FCSTD DOCUMENT  (FreeCAD 0.16R6706 (Git))
Label: side-mount-btm
License: All rights reserved
LicenseURL: http://en.wikipedia.org/wiki/All_rights_reserved
objects: Sketcher::SketchObject×17, PartDesign::Pocket×17, App::DocumentObjectGroup×7, PartDesign::Fillet×7, Part::Box×5, Mesh::Feature×4
note: 63 computed .brp shape members not serialized (recipe doc carries the construction recipe); baked Part::Feature solids carry a one-line shape summary decoded from their .brp

FEATURE [Part::Box] Box  label="Cube"
  Height = 16.1
  Length = 52
  Width = 38
FEATURE [Sketcher::SketchObject] Sketch003  label="rail holes"
  Placement = pos=(0,38,0) rot=(0,0.707107,0.707107;3.14159rad)
  Support = -> Box [Face4]
  sketch-geometry (6):
    g0: Circle CenterX=-46 CenterY=8.25 CenterZ=0 NormalX=0 NormalY=0 NormalZ=1 Radius=4.2
    g1: Circle CenterX=-6 CenterY=8.25 CenterZ=0 NormalX=0 NormalY=0 NormalZ=1 Radius=4.2
    g2: LineSegment StartX=-35.5 StartY=13.1 StartZ=0 EndX=-16.5 EndY=13.1 EndZ=0
    g3: LineSegment StartX=-16.5 StartY=13.1 StartZ=0 EndX=-16.5 EndY=3.1 EndZ=0
    g4: LineSegment StartX=-16.5 StartY=3.1 StartZ=0 EndX=-35.5 EndY=3.1 EndZ=0
    g5: LineSegment StartX=-35.5 StartY=3.1 StartZ=0 EndX=-35.5 EndY=13.1 EndZ=0
  constraints (18):
    c: Equal(g1,g0)
    c: Radius(g0) = 4.2
    c: Distance(g0,g1) = 40
    c: DistanceY(g-1,g0) = 8.25
    c: DistanceY(g-1,g1) = 8.25
    c: DistanceX(g-2,g1) = -6
    c: Coincident(g2,g3)
    c: Coincident(g3,g4)
    c: Coincident(g4,g5)
    c: Coincident(g5,g2)
    c: Horizontal(g2)
    c: Horizontal(g4)
    c: Vertical(g3)
    c: Vertical(g5)
    c: Distance(g4) = 19
    c: DistanceX(g-2,g2) = -16.5
    c: DistanceY(g-1,g3) = 3.1
    c: Distance(g2,g4) = 10
FEATURE [PartDesign::Pocket] Pocket
  Length = 5
  Sketch = -> Sketch003
  Type = 1
FEATURE [Sketcher::SketchObject] Sketch007  label="mounting holes"
  Placement = pos=(0,0,16.1) rot=(0,0,1;0rad)
  Support = -> Pocket [Face3]
  sketch-geometry (4):
    g0: Circle CenterX=13 CenterY=5 CenterZ=0 NormalX=0 NormalY=0 NormalZ=1 Radius=1.4
    g1: Circle CenterX=39 CenterY=5 CenterZ=0 NormalX=0 NormalY=0 NormalZ=1 Radius=1.4
    g2: Circle CenterX=39 CenterY=33 CenterZ=0 NormalX=0 NormalY=0 NormalZ=1 Radius=1.4
    g3: Circle CenterX=13 CenterY=33 CenterZ=0 NormalX=0 NormalY=0 NormalZ=1 Radius=1.4
  constraints (12):
    c: Radius(g1) = 1.4
    c: Equal(g1,g0)
    c: Equal(g0,g3)
    c: Equal(g3,g2)
    c: DistanceY(g-1,g1) = 5
    c: DistanceY(g-1,g0) = 5
    c: DistanceX(g-2,g0) = 13
    c: DistanceX(g-2,g3) = 13
    c: Distance(g0,g3) = 28
    c: Distance(g1,g2) = 28
    c: Distance(g0,g1) = 26
    c: Distance(g3,g2) = 26
FEATURE [PartDesign::Pocket] Pocket001
  Length = 8
  Sketch = -> Sketch007
  Type = 1
FEATURE [Sketcher::SketchObject] Sketch008  label="rail set screw holes2"
  Placement = pos=(0,0,0) rot=(0.57735,-0.57735,-0.57735;2.0944rad)
  Support = -> Pocket001 [Face1]
  sketch-geometry (2):
    g0: Circle CenterX=-29.5 CenterY=8.25 CenterZ=0 NormalX=0 NormalY=0 NormalZ=1 Radius=1.5
    g1: Circle CenterX=-9.5 CenterY=8.25 CenterZ=0 NormalX=0 NormalY=0 NormalZ=1 Radius=1.5
  constraints (6):
    c: Radius(g0) = 1.5
    c: Equal(g0,g1)
    c: DistanceY(g-1,g0) = 8.25
    c: DistanceY(g-1,g1) = 8.25
    c: Distance(g0,g1) = 20
    c: DistanceX(g-2,g1) = -9.5
FEATURE [PartDesign::Pocket] Pocket002
  Length = 3
  Sketch = -> Sketch008
  Type = 0
FEATURE [Sketcher::SketchObject] Sketch004  label="rail set screw holes"
  Placement = pos=(52,0,0) rot=(0.57735,0.57735,0.57735;2.0944rad)
  Support = -> Pocket002 [Face8]
  sketch-geometry (2):
    g0: Circle CenterX=9.5 CenterY=8.25 CenterZ=0 NormalX=0 NormalY=0 NormalZ=1 Radius=1.5
    g1: Circle CenterX=29.5 CenterY=8.25 CenterZ=0 NormalX=0 NormalY=0 NormalZ=1 Radius=1.5
  constraints (6):
    c: Radius(g0) = 1.5
    c: Equal(g0,g1)
    c: DistanceY(g-1,g0) = 8.25
    c: DistanceY(g-1,g1) = 8.25
    c: Distance(g0,g1) = 20
    c: DistanceX(g-2,g0) = 9.5
FEATURE [PartDesign::Pocket] Pocket003
  Length = 3
  Sketch = -> Sketch004
  Type = 0
FEATURE [Sketcher::SketchObject] Sketch013  label="pulley hole"
  Placement = pos=(0,0,16.1) rot=(0,0,1;0rad)
  Support = -> Pocket003 [Face3]
  sketch-geometry (1):
    g0: Circle CenterX=26 CenterY=4 CenterZ=0 NormalX=0 NormalY=0 NormalZ=1 Radius=1.68
  constraints (3):
    c: DistanceX(g-2,g0) = 26
    c: DistanceY(g-1,g0) = 4
    c: Radius(g0) = 1.68
FEATURE [PartDesign::Pocket] Pocket004
  Length = 5
  Sketch = -> Sketch013
  Type = 1
FEATURE [Mesh::Feature] side_mnt_top  label="side-mnt-top"
  Placement = pos=(4.5,-38,16) rot=(0,0,1;0rad)
FEATURE [Mesh::Feature] side_mnt_top001  label="side-mnt-top001"
  Placement = pos=(30.5,-38,16) rot=(0,0,1;0rad)
FEATURE [App::DocumentObjectGroup] Group002  label="bearing mounts"
  Group = -> [side_mnt_top,side_mnt_top001]
FEATURE [Part::Box] Box001  label="pulley block"
  Height = 13
  Length = 36
  Placement = pos=(8,-13,-13) rot=(0,0,1;0rad)
  Width = 25
FEATURE [Sketcher::SketchObject] Sketch
  Placement = pos=(8,-13,-13) rot=(1,0,0;3.14159rad)
  Support = -> Box001 [Face5]
  sketch-geometry (3):
    g0: Circle CenterX=31 CenterY=-18 CenterZ=0 NormalX=0 NormalY=0 NormalZ=1 Radius=1.68
    g1: Circle CenterX=5 CenterY=-18 CenterZ=0 NormalX=0 NormalY=0 NormalZ=1 Radius=1.68
    g2: Circle CenterX=18 CenterY=-3.8 CenterZ=0 NormalX=0 NormalY=0 NormalZ=1 Radius=1.68
  constraints (9):
    c: Radius(g1) = 1.68
    c: Equal(g1,g0)
    c: DistanceX(g-2,g1) = 5
    c: DistanceY(g-1,g1) = -18
    c: DistanceY(g-1,g0) = -18
    c: Distance(g1,g0) = 26
    c: Equal(g2,g1)
    c: DistanceX(g-2,g2) = 18
    c: DistanceY(g-1,g2) = -3.8
FEATURE [PartDesign::Pocket] Pocket005
  Length = 5
  Placement = pos=(8,-13,-13) rot=(0,0,1;0rad)
  Sketch = -> Sketch
  Type = 1
FEATURE [Sketcher::SketchObject] Sketch014
  Placement = pos=(8,-13,-13) rot=(0.57735,-0.57735,-0.57735;2.0944rad)
  Support = -> Pocket005 [Face1]
  sketch-geometry (4):
    g0: LineSegment StartX=-13 StartY=13 StartZ=0 EndX=0 EndY=13 EndZ=0
    g1: LineSegment StartX=0 StartY=13 StartZ=0 EndX=0 EndY=3 EndZ=0
    g2: LineSegment StartX=0 StartY=3 StartZ=0 EndX=-13 EndY=3 EndZ=0
    g3: LineSegment StartX=-13 StartY=3 StartZ=0 EndX=-13 EndY=13 EndZ=0
  constraints (12):
    c: Coincident(g0,g1)
    c: Coincident(g1,g2)
    c: Coincident(g2,g3)
    c: Coincident(g3,g0)
    c: Horizontal(g0)
    c: Horizontal(g2)
    c: Vertical(g1)
    c: Vertical(g3)
    c: DistanceY(g-1,g1) = 3
    c: DistanceX(g-2,g0) = 0
    c: Distance(g3) = 10
    c: Distance(g0) = 13
FEATURE [PartDesign::Pocket] Pocket006
  Length = 5
  Placement = pos=(8,-13,-13) rot=(0,0,1;0rad)
  Sketch = -> Sketch014
  Type = 1
FEATURE [Sketcher::SketchObject] Sketch015
  Placement = pos=(8,-13,-13) rot=(1,0,0;3.14159rad)
  Support = -> Pocket006 [Face7]
  sketch-geometry (2):
    g0: Circle CenterX=5 CenterY=-18 CenterZ=0 NormalX=0 NormalY=0 NormalZ=1 Radius=3
    g1: Circle CenterX=31 CenterY=-18 CenterZ=0 NormalX=0 NormalY=0 NormalZ=1 Radius=3
  constraints (6):
    c: Distance(g0,g1) = 26
    c: Radius(g0) = 3
    c: Equal(g0,g1)
    c: DistanceX(g-2,g0) = 5
    c: DistanceY(g-1,g0) = -18
    c: DistanceY(g-1,g1) = -18
FEATURE [PartDesign::Pocket] Pocket007  label="countersinks"
  Length = 4
  Placement = pos=(8,-13,-13) rot=(0,0,1;0rad)
  Sketch = -> Sketch015
  Type = 0
FEATURE [Sketcher::SketchObject] Sketch016
  Placement = pos=(8,-13,0) rot=(0,0,1;0rad)
  Support = -> Pocket007 [Face5]
  sketch-geometry (3):
    g0: LineSegment StartX=8.5 StartY=13 StartZ=0 EndX=18 EndY=22 EndZ=0
    g1: LineSegment StartX=18 StartY=22 StartZ=0 EndX=27.5 EndY=13 EndZ=0
    g2: LineSegment StartX=27.5 StartY=13 StartZ=0 EndX=8.5 EndY=13 EndZ=0
  constraints (9):
    c: Coincident(g0,g1)
    c: Coincident(g1,g2)
    c: Coincident(g2,g0)
    c: Distance(g2) = 19
    c: DistanceX(g-2,g2) = 8.5
    c: DistanceY(g-1,g0) = 13
    c: DistanceX(g-2,g0) = 18
    c: DistanceY(g-1,g0) = 22
    c: DistanceY(g-1,g1) = 13
FEATURE [PartDesign::Pocket] Pocket008
  Length = 10
  Placement = pos=(8,-13,-13) rot=(0,0,1;0rad)
  Sketch = -> Sketch016
  Type = 0
FEATURE [PartDesign::Fillet] Fillet
  Base = -> Pocket008 [Edge16,Edge33]
  Placement = pos=(8,-13,-13) rot=(0,0,1;0rad)
  Radius = 18
FEATURE [PartDesign::Fillet] Fillet001
  Base = -> Fillet [Edge39]
  Placement = pos=(8,-13,-13) rot=(0,0,1;0rad)
  Radius = 4.5
FEATURE [PartDesign::Fillet] Fillet002
  Base = -> Fillet001 [Edge37,Edge34]
  Placement = pos=(8,-13,-13) rot=(0,0,1;0rad)
  Radius = 13.9
FEATURE [App::DocumentObjectGroup] Group003  label="pulley mnt"
  Group = -> [Box001,Pocket005,Pocket006,Pocket007,Pocket008,Fillet,Fillet001,Fillet002]
FEATURE [Part::Box] Box002  label="Cube001"
  Height = 3.1
  Length = 28
  Placement = pos=(12,-13,0) rot=(0,0,1;0rad)
  Width = 14
FEATURE [Sketcher::SketchObject] Sketch017
  Placement = pos=(12,-13,0) rot=(1,0,0;3.14159rad)
  Support = -> Box002 [Face5]
  sketch-geometry (1):
    g0: Circle CenterX=14 CenterY=-3.8 CenterZ=0 NormalX=0 NormalY=0 NormalZ=1 Radius=1.68
  constraints (3):
    c: Radius(g0) = 1.68
    c: DistanceX(g-2,g0) = 14
    c: DistanceY(g-1,g0) = -3.8
FEATURE [PartDesign::Pocket] Pocket009
  Length = 5
  Placement = pos=(12,-13,0) rot=(0,0,1;0rad)
  Sketch = -> Sketch017
  Type = 0
FEATURE [PartDesign::Fillet] Fillet003
  Base = -> Pocket009 [Edge6,Edge1]
  Placement = pos=(12,-13,0) rot=(0,0,1;0rad)
  Radius = 13
FEATURE [App::DocumentObjectGroup] Group004  label="pulley mnt 1"
  Group = -> [Box002,Pocket009,Fillet003]
FEATURE [PartDesign::Fillet] Fillet004
  Base = -> Pocket004 [Edge17,Edge24,Edge2,Edge3]
  Radius = 5
FEATURE [App::DocumentObjectGroup] Group  label="right"
  Group = -> [Box,Pocket,Pocket001,Pocket002,Pocket003,Pocket004,Group003,Group004,Fillet004]
FEATURE [Part::Box] Box003  label="Cube002"
  Height = 16.1
  Length = 52
  Placement = pos=(70,0,0) rot=(0,0,1;0rad)
  Width = 38
FEATURE [Sketcher::SketchObject] Sketch018  label="rail holes001"
  Placement = pos=(70,38,0) rot=(0,0.707107,0.707107;3.14159rad)
  Support = -> Box003 [Face4]
  sketch-geometry (6):
    g0: Circle CenterX=-46 CenterY=8.25 CenterZ=0 NormalX=0 NormalY=0 NormalZ=1 Radius=4.2
    g1: Circle CenterX=-6 CenterY=8.25 CenterZ=0 NormalX=0 NormalY=0 NormalZ=1 Radius=4.2
    g2: LineSegment StartX=-35.5 StartY=13.1 StartZ=0 EndX=-16.5 EndY=13.1 EndZ=0
    g3: LineSegment StartX=-16.5 StartY=13.1 StartZ=0 EndX=-16.5 EndY=3.1 EndZ=0
    g4: LineSegment StartX=-16.5 StartY=3.1 StartZ=0 EndX=-35.5 EndY=3.1 EndZ=0
    g5: LineSegment StartX=-35.5 StartY=3.1 StartZ=0 EndX=-35.5 EndY=13.1 EndZ=0
  constraints (18):
    c: Equal(g1,g0)
    c: Radius(g0) = 4.2
    c: Distance(g0,g1) = 40
    c: DistanceY(g-1,g0) = 8.25
    c: DistanceY(g-1,g1) = 8.25
    c: DistanceX(g-2,g1) = -6
    c: Coincident(g2,g3)
    c: Coincident(g3,g4)
    c: Coincident(g4,g5)
    c: Coincident(g5,g2)
    c: Horizontal(g2)
    c: Horizontal(g4)
    c: Vertical(g3)
    c: Vertical(g5)
    c: Distance(g4) = 19
    c: DistanceX(g-2,g2) = -16.5
    c: DistanceY(g-1,g3) = 3.1
    c: Distance(g2,g4) = 10
FEATURE [PartDesign::Pocket] Pocket010
  Length = 5
  Placement = pos=(70,0,0) rot=(0,0,1;0rad)
  Sketch = -> Sketch018
  Type = 1
FEATURE [Sketcher::SketchObject] Sketch020  label="mounting holes001"
  Placement = pos=(70,0,16.1) rot=(0,0,1;0rad)
  Support = -> Pocket010 [Face3]
  sketch-geometry (6):
    g0: Circle CenterX=13 CenterY=5 CenterZ=0 NormalX=0 NormalY=0 NormalZ=1 Radius=1.4
    g1: Circle CenterX=39 CenterY=5 CenterZ=0 NormalX=0 NormalY=0 NormalZ=1 Radius=1.4
    g2: Circle CenterX=39 CenterY=33 CenterZ=0 NormalX=0 NormalY=0 NormalZ=1 Radius=1.4
    g3: Circle CenterX=13 CenterY=33 CenterZ=0 NormalX=0 NormalY=0 NormalZ=1 Radius=1.4
    g4: Circle CenterX=26 CenterY=4 CenterZ=0 NormalX=0 NormalY=0 NormalZ=1 Radius=1.68
    g5: Circle CenterX=26 CenterY=17.2 CenterZ=0 NormalX=0 NormalY=0 NormalZ=1 Radius=1.68
  constraints (18):
    c: Radius(g1) = 1.4
    c: Equal(g1,g0)
    c: Equal(g0,g3)
    c: Equal(g3,g2)
    c: DistanceY(g-1,g1) = 5
    c: DistanceY(g-1,g0) = 5
    c: DistanceX(g-2,g0) = 13
    c: DistanceX(g-2,g3) = 13
    c: Distance(g0,g3) = 28
    c: Distance(g1,g2) = 28
    c: Distance(g0,g1) = 26
    c: Distance(g3,g2) = 26
    c: Radius(g4) = 1.68
    c: DistanceY(g-1,g4) = 4
    c: DistanceX(g-2,g4) = 26
    c: Equal(g4,g5)
    c: DistanceX(g-2,g5) = 26
    c: Distance(g5,g4) = 13.2
FEATURE [PartDesign::Pocket] Pocket011
  Length = 8
  Placement = pos=(70,0,0) rot=(0,0,1;0rad)
  Sketch = -> Sketch020
  Type = 1
FEATURE [Sketcher::SketchObject] Sketch021  label="rail set screw holes004"
  Placement = pos=(70,0,0) rot=(0.57735,-0.57735,-0.57735;2.0944rad)
  Support = -> Pocket011 [Face1]
  sketch-geometry (2):
    g0: Circle CenterX=-29.5 CenterY=8.25 CenterZ=0 NormalX=0 NormalY=0 NormalZ=1 Radius=1.5
    g1: Circle CenterX=-9.5 CenterY=8.25 CenterZ=0 NormalX=0 NormalY=0 NormalZ=1 Radius=1.5
  constraints (6):
    c: Radius(g0) = 1.5
    c: Equal(g0,g1)
    c: DistanceY(g-1,g0) = 8.25
    c: DistanceY(g-1,g1) = 8.25
    c: Distance(g0,g1) = 20
    c: DistanceX(g-2,g1) = -9.5
FEATURE [PartDesign::Pocket] Pocket012
  Length = 3
  Placement = pos=(70,0,0) rot=(0,0,1;0rad)
  Sketch = -> Sketch021
  Type = 0
FEATURE [Sketcher::SketchObject] Sketch019  label="rail set screw holes003"
  Placement = pos=(122,0,0) rot=(0.57735,0.57735,0.57735;2.0944rad)
  Support = -> Pocket012 [Face8]
  sketch-geometry (2):
    g0: Circle CenterX=9.5 CenterY=8.25 CenterZ=0 NormalX=0 NormalY=0 NormalZ=1 Radius=1.5
    g1: Circle CenterX=29.5 CenterY=8.25 CenterZ=0 NormalX=0 NormalY=0 NormalZ=1 Radius=1.5
  constraints (6):
    c: Radius(g0) = 1.5
    c: Equal(g0,g1)
    c: DistanceY(g-1,g0) = 8.25
    c: DistanceY(g-1,g1) = 8.25
    c: Distance(g0,g1) = 20
    c: DistanceX(g-2,g0) = 9.5
FEATURE [PartDesign::Pocket] Pocket013  label="main frame"
  Length = 3
  Placement = pos=(70,0,0) rot=(0,0,1;0rad)
  Sketch = -> Sketch019
  Type = 0
FEATURE [Part::Box] Box004  label="Cube003"
  Height = 14
  Length = 16
  Placement = pos=(87,12,-14) rot=(0,0,1;0rad)
  Width = 26
FEATURE [Sketcher::SketchObject] Sketch023
  Placement = pos=(87,12,-14) rot=(1,0,0;3.14159rad)
  Support = -> Box004 [Face5]
  sketch-geometry (1):
    g0: Circle CenterX=9 CenterY=-5.2 CenterZ=0 NormalX=0 NormalY=0 NormalZ=1 Radius=1.68
  constraints (3):
    c: Radius(g0) = 1.68
    c: DistanceX(g-2,g0) = 9
    c: DistanceY(g-1,g0) = -5.2
FEATURE [PartDesign::Pocket] Pocket014
  Length = 19
  Placement = pos=(87,12,-14) rot=(0,0,1;0rad)
  Sketch = -> Sketch023
  Type = 0
FEATURE [Sketcher::SketchObject] Sketch022
  Placement = pos=(87,12,0) rot=(0,0,1;0rad)
  Support = -> Pocket014 [Face3]
  sketch-geometry (1):
    g0: Circle CenterX=9 CenterY=5.2 CenterZ=0 NormalX=0 NormalY=0 NormalZ=1 Radius=10.6
  constraints (3):
    c: Radius(g0) = 10.6
    c: DistanceY(g-1,g0) = 5.2
    c: DistanceX(g-2,g0) = 9
FEATURE [PartDesign::Pocket] Pocket015
  Length = 10
  Placement = pos=(87,12,-14) rot=(0,0,1;0rad)
  Sketch = -> Sketch022
  Type = 0
FEATURE [PartDesign::Fillet] Fillet006
  Base = -> Pocket013 [Edge17,Edge25,Edge3,Edge2]
  Placement = pos=(70,0,0) rot=(0,0,1;0rad)
  Radius = 5
FEATURE [Mesh::Feature] side_mnt_top004  label="side-mnt-top004"
  Placement = pos=(74.5,-38,16) rot=(0,0,1;0rad)
FEATURE [Mesh::Feature] side_mnt_top005  label="side-mnt-top005"
  Placement = pos=(100.5,-38,16) rot=(0,0,1;0rad)
FEATURE [App::DocumentObjectGroup] Group007  label="bearing mounts002"
  Group = -> [side_mnt_top004,side_mnt_top005]
FEATURE [Sketcher::SketchObject] Sketch024
  Placement = pos=(103,12,-14) rot=(0.57735,0.57735,0.57735;2.0944rad)
  Support = -> Pocket015 [Face8]
  sketch-geometry (4):
    g0: LineSegment StartX=13 StartY=4 StartZ=0 EndX=26 EndY=4 EndZ=0
    g1: LineSegment StartX=26 StartY=4 StartZ=0 EndX=26 EndY=14 EndZ=0
    g2: LineSegment StartX=26 StartY=14 StartZ=0 EndX=13 EndY=14 EndZ=0
    g3: LineSegment StartX=13 StartY=14 StartZ=0 EndX=13 EndY=4 EndZ=0
  constraints (12):
    c: Coincident(g0,g1)
    c: Coincident(g1,g2)
    c: Coincident(g2,g3)
    c: Coincident(g3,g0)
    c: Horizontal(g0)
    c: Horizontal(g2)
    c: Vertical(g1)
    c: Vertical(g3)
    c: DistanceY(g-1,g0) = 4
    c: Distance(g1) = 10
    c: DistanceX(g-2,g0) = 13
    c: Distance(g0) = 13
FEATURE [PartDesign::Pocket] Pocket016
  Length = 3
  Placement = pos=(87,12,-14) rot=(0,0,1;0rad)
  Sketch = -> Sketch024
  Type = 0
FEATURE [PartDesign::Fillet] Fillet007
  Base = -> Pocket016 [Edge1,Edge7]
  Placement = pos=(87,12,-14) rot=(0,0,1;0rad)
  Radius = 7.8
FEATURE [App::DocumentObjectGroup] Group005  label="pulley mount"
  Group = -> [Box004,Pocket014,Pocket015,Group007,Pocket016,Fillet007]
FEATURE [App::DocumentObjectGroup] Group001  label="left"
  Group = -> [Box003,Pocket013,Pocket010,Pocket012,Pocket011,Group005,Fillet006]
